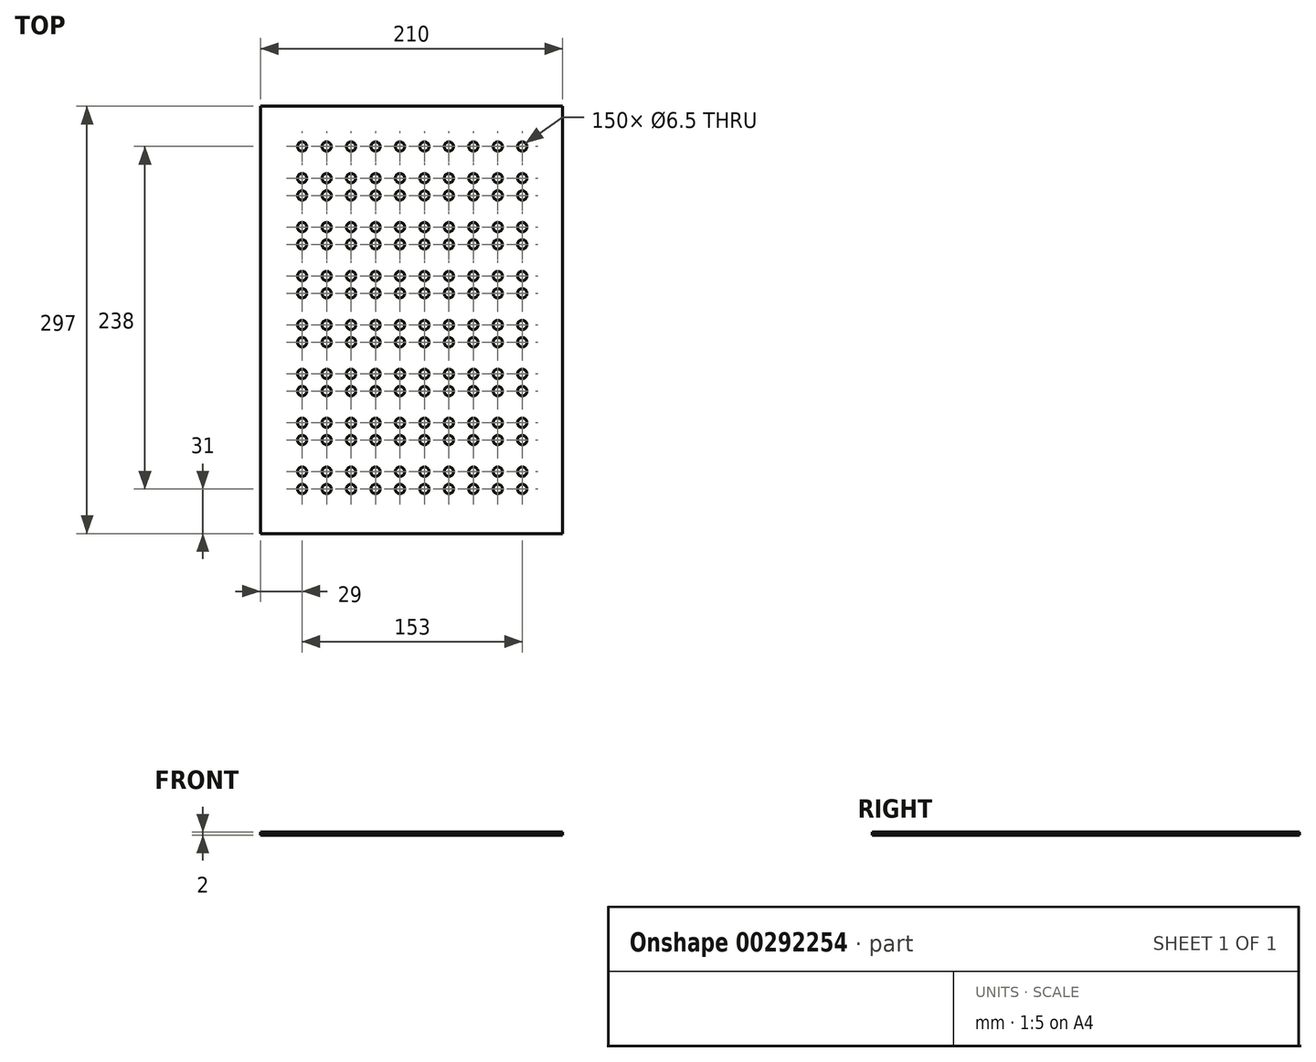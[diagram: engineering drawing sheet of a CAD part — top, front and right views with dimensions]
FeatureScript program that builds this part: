
annotation { "Feature Type Name" : "Feature", "Feature Type Description" : "" }
export const myFeature = defineFeature(function(context is Context, id is Id, definition is map)
    precondition{}
    {
        {
            var Q0;
            Q0=qCreatedBy(makeId("Top.planeOp"),FACE);
            var sketch = newSketch(context, id + "F0", { "sketchPlane" : qUnion([Q0])});
            skLineSegment(sketch, "E0.bottom", {"start": v(-105, 148.5) * mm, "end": v(105, 148.5) * mm});
            skLineSegment(sketch, "E0.top", {"start": v(-105, -148.5) * mm, "end": v(105, -148.5) * mm});
            skLineSegment(sketch, "E0.left", {"start": v(-105, 148.5) * mm, "end": v(-105, -148.5) * mm});
            skLineSegment(sketch, "E0.right", {"start": v(105, 148.5) * mm, "end": v(105, -148.5) * mm});
            skCircle(sketch, "E1", {"center": v(-76, 98.5) * mm, "radius": 3.25 * mm});
            skCircle(sketch, "E2.0.1.0", {"center": v(-76, 86.5) * mm, "radius": 3.25 * mm});
            skCircle(sketch, "E2.1.0.0", {"center": v(-59, 98.5) * mm, "radius": 3.25 * mm});
            skCircle(sketch, "E2.1.1.0", {"center": v(-59, 86.5) * mm, "radius": 3.25 * mm});
            skCircle(sketch, "E2.2.0.0", {"center": v(-42, 98.5) * mm, "radius": 3.25 * mm});
            skCircle(sketch, "E2.2.1.0", {"center": v(-42, 86.5) * mm, "radius": 3.25 * mm});
            skCircle(sketch, "E2.3.0.0", {"center": v(-25, 98.5) * mm, "radius": 3.25 * mm});
            skCircle(sketch, "E2.3.1.0", {"center": v(-25, 86.5) * mm, "radius": 3.25 * mm});
            skCircle(sketch, "E2.4.0.0", {"center": v(-8, 98.5) * mm, "radius": 3.25 * mm});
            skCircle(sketch, "E2.4.1.0", {"center": v(-8, 86.5) * mm, "radius": 3.25 * mm});
            skCircle(sketch, "E2.5.0.0", {"center": v(9, 98.5) * mm, "radius": 3.25 * mm});
            skCircle(sketch, "E2.5.1.0", {"center": v(9, 86.5) * mm, "radius": 3.25 * mm});
            skCircle(sketch, "E2.6.0.0", {"center": v(26, 98.5) * mm, "radius": 3.25 * mm});
            skCircle(sketch, "E2.6.1.0", {"center": v(26, 86.5) * mm, "radius": 3.25 * mm});
            skCircle(sketch, "E2.7.0.0", {"center": v(43, 98.5) * mm, "radius": 3.25 * mm});
            skCircle(sketch, "E2.7.1.0", {"center": v(43, 86.5) * mm, "radius": 3.25 * mm});
            skLineSegment(sketch, "E2.direction1", {"start": v(-76, 98.5) * mm, "end": v(-59, 98.5) * mm, "construction": true});
            skLineSegment(sketch, "E2.direction2", {"start": v(-76, 98.5) * mm, "end": v(-76, 86.5) * mm, "construction": true});
            skCircle(sketch, "E3", {"center": v(-76, 64.5) * mm, "radius": 3.25 * mm});
            skCircle(sketch, "E4.0.1.0", {"center": v(-76, 52.5) * mm, "radius": 3.25 * mm});
            skCircle(sketch, "E4.1.0.0", {"center": v(-59, 64.5) * mm, "radius": 3.25 * mm});
            skCircle(sketch, "E4.1.1.0", {"center": v(-59, 52.5) * mm, "radius": 3.25 * mm});
            skCircle(sketch, "E4.2.0.0", {"center": v(-42, 64.5) * mm, "radius": 3.25 * mm});
            skCircle(sketch, "E4.2.1.0", {"center": v(-42, 52.5) * mm, "radius": 3.25 * mm});
            skCircle(sketch, "E4.3.0.0", {"center": v(-25, 64.5) * mm, "radius": 3.25 * mm});
            skCircle(sketch, "E4.3.1.0", {"center": v(-25, 52.5) * mm, "radius": 3.25 * mm});
            skCircle(sketch, "E4.4.0.0", {"center": v(-8, 64.5) * mm, "radius": 3.25 * mm});
            skCircle(sketch, "E4.4.1.0", {"center": v(-8, 52.5) * mm, "radius": 3.25 * mm});
            skCircle(sketch, "E4.5.0.0", {"center": v(9, 64.5) * mm, "radius": 3.25 * mm});
            skCircle(sketch, "E4.5.1.0", {"center": v(9, 52.5) * mm, "radius": 3.25 * mm});
            skCircle(sketch, "E4.6.0.0", {"center": v(26, 64.5) * mm, "radius": 3.25 * mm});
            skCircle(sketch, "E4.6.1.0", {"center": v(26, 52.5) * mm, "radius": 3.25 * mm});
            skCircle(sketch, "E4.7.0.0", {"center": v(43, 64.5) * mm, "radius": 3.25 * mm});
            skCircle(sketch, "E4.7.1.0", {"center": v(43, 52.5) * mm, "radius": 3.25 * mm});
            skLineSegment(sketch, "E4.direction1", {"start": v(-76, 64.5) * mm, "end": v(-59, 64.5) * mm, "construction": true});
            skLineSegment(sketch, "E4.direction2", {"start": v(-76, 64.5) * mm, "end": v(-76, 52.5) * mm, "construction": true});
            skCircle(sketch, "E5", {"center": v(-76, 30.5) * mm, "radius": 3.25 * mm});
            skCircle(sketch, "E6.0.1.0", {"center": v(-76, 18.5) * mm, "radius": 3.25 * mm});
            skCircle(sketch, "E6.1.0.0", {"center": v(-59, 30.5) * mm, "radius": 3.25 * mm});
            skCircle(sketch, "E6.1.1.0", {"center": v(-59, 18.5) * mm, "radius": 3.25 * mm});
            skCircle(sketch, "E6.2.0.0", {"center": v(-42, 30.5) * mm, "radius": 3.25 * mm});
            skCircle(sketch, "E6.2.1.0", {"center": v(-42, 18.5) * mm, "radius": 3.25 * mm});
            skCircle(sketch, "E6.3.0.0", {"center": v(-25, 30.5) * mm, "radius": 3.25 * mm});
            skCircle(sketch, "E6.3.1.0", {"center": v(-25, 18.5) * mm, "radius": 3.25 * mm});
            skCircle(sketch, "E6.4.0.0", {"center": v(-8, 30.5) * mm, "radius": 3.25 * mm});
            skCircle(sketch, "E6.4.1.0", {"center": v(-8, 18.5) * mm, "radius": 3.25 * mm});
            skCircle(sketch, "E6.5.0.0", {"center": v(9, 30.5) * mm, "radius": 3.25 * mm});
            skCircle(sketch, "E6.5.1.0", {"center": v(9, 18.5) * mm, "radius": 3.25 * mm});
            skCircle(sketch, "E6.6.0.0", {"center": v(26, 30.5) * mm, "radius": 3.25 * mm});
            skCircle(sketch, "E6.6.1.0", {"center": v(26, 18.5) * mm, "radius": 3.25 * mm});
            skCircle(sketch, "E6.7.0.0", {"center": v(43, 30.5) * mm, "radius": 3.25 * mm});
            skCircle(sketch, "E6.7.1.0", {"center": v(43, 18.5) * mm, "radius": 3.25 * mm});
            skLineSegment(sketch, "E6.direction1", {"start": v(-76, 30.5) * mm, "end": v(-59, 30.5) * mm, "construction": true});
            skLineSegment(sketch, "E6.direction2", {"start": v(-76, 30.5) * mm, "end": v(-76, 18.5) * mm, "construction": true});
            skCircle(sketch, "E7", {"center": v(-76, -3.5) * mm, "radius": 3.25 * mm});
            skCircle(sketch, "E8.0.1.0", {"center": v(-76, -15.5) * mm, "radius": 3.25 * mm});
            skCircle(sketch, "E8.1.0.0", {"center": v(-59, -3.5) * mm, "radius": 3.25 * mm});
            skCircle(sketch, "E8.1.1.0", {"center": v(-59, -15.5) * mm, "radius": 3.25 * mm});
            skCircle(sketch, "E8.2.0.0", {"center": v(-42, -3.5) * mm, "radius": 3.25 * mm});
            skCircle(sketch, "E8.2.1.0", {"center": v(-42, -15.5) * mm, "radius": 3.25 * mm});
            skCircle(sketch, "E8.3.0.0", {"center": v(-25, -3.5) * mm, "radius": 3.25 * mm});
            skCircle(sketch, "E8.3.1.0", {"center": v(-25, -15.5) * mm, "radius": 3.25 * mm});
            skCircle(sketch, "E8.4.0.0", {"center": v(-8, -3.5) * mm, "radius": 3.25 * mm});
            skCircle(sketch, "E8.4.1.0", {"center": v(-8, -15.5) * mm, "radius": 3.25 * mm});
            skCircle(sketch, "E8.5.0.0", {"center": v(9, -3.5) * mm, "radius": 3.25 * mm});
            skCircle(sketch, "E8.5.1.0", {"center": v(9, -15.5) * mm, "radius": 3.25 * mm});
            skCircle(sketch, "E8.6.0.0", {"center": v(26, -3.5) * mm, "radius": 3.25 * mm});
            skCircle(sketch, "E8.6.1.0", {"center": v(26, -15.5) * mm, "radius": 3.25 * mm});
            skCircle(sketch, "E8.7.0.0", {"center": v(43, -3.5) * mm, "radius": 3.25 * mm});
            skCircle(sketch, "E8.7.1.0", {"center": v(43, -15.5) * mm, "radius": 3.25 * mm});
            skLineSegment(sketch, "E8.direction1", {"start": v(-76, -3.5) * mm, "end": v(-59, -3.5) * mm, "construction": true});
            skLineSegment(sketch, "E8.direction2", {"start": v(-76, -3.5) * mm, "end": v(-76, -15.5) * mm, "construction": true});
            skCircle(sketch, "E9", {"center": v(-76, -37.5) * mm, "radius": 3.25 * mm});
            skCircle(sketch, "E10.0.1.0", {"center": v(-76, -49.5) * mm, "radius": 3.25 * mm});
            skCircle(sketch, "E10.1.0.0", {"center": v(-59, -37.5) * mm, "radius": 3.25 * mm});
            skCircle(sketch, "E10.1.1.0", {"center": v(-59, -49.5) * mm, "radius": 3.25 * mm});
            skCircle(sketch, "E10.2.0.0", {"center": v(-42, -37.5) * mm, "radius": 3.25 * mm});
            skCircle(sketch, "E10.2.1.0", {"center": v(-42, -49.5) * mm, "radius": 3.25 * mm});
            skCircle(sketch, "E10.3.0.0", {"center": v(-25, -37.5) * mm, "radius": 3.25 * mm});
            skCircle(sketch, "E10.3.1.0", {"center": v(-25, -49.5) * mm, "radius": 3.25 * mm});
            skCircle(sketch, "E10.4.0.0", {"center": v(-8, -37.5) * mm, "radius": 3.25 * mm});
            skCircle(sketch, "E10.4.1.0", {"center": v(-8, -49.5) * mm, "radius": 3.25 * mm});
            skCircle(sketch, "E10.5.0.0", {"center": v(9, -37.5) * mm, "radius": 3.25 * mm});
            skCircle(sketch, "E10.5.1.0", {"center": v(9, -49.5) * mm, "radius": 3.25 * mm});
            skCircle(sketch, "E10.6.0.0", {"center": v(26, -37.5) * mm, "radius": 3.25 * mm});
            skCircle(sketch, "E10.6.1.0", {"center": v(26, -49.5) * mm, "radius": 3.25 * mm});
            skCircle(sketch, "E10.7.0.0", {"center": v(43, -37.5) * mm, "radius": 3.25 * mm});
            skCircle(sketch, "E10.7.1.0", {"center": v(43, -49.5) * mm, "radius": 3.25 * mm});
            skLineSegment(sketch, "E10.direction1", {"start": v(-76, -37.5) * mm, "end": v(-59, -37.5) * mm, "construction": true});
            skLineSegment(sketch, "E10.direction2", {"start": v(-76, -37.5) * mm, "end": v(-76, -49.5) * mm, "construction": true});
            skCircle(sketch, "E11", {"center": v(-76, 120.5) * mm, "radius": 3.25 * mm});
            skCircle(sketch, "E12.1.0.0", {"center": v(-59, 120.5) * mm, "radius": 3.25 * mm});
            skCircle(sketch, "E12.2.0.0", {"center": v(-42, 120.5) * mm, "radius": 3.25 * mm});
            skCircle(sketch, "E12.3.0.0", {"center": v(-25, 120.5) * mm, "radius": 3.25 * mm});
            skCircle(sketch, "E12.4.0.0", {"center": v(-8, 120.5) * mm, "radius": 3.25 * mm});
            skCircle(sketch, "E12.5.0.0", {"center": v(9, 120.5) * mm, "radius": 3.25 * mm});
            skCircle(sketch, "E12.6.0.0", {"center": v(26, 120.5) * mm, "radius": 3.25 * mm});
            skCircle(sketch, "E12.7.0.0", {"center": v(43, 120.5) * mm, "radius": 3.25 * mm});
            skLineSegment(sketch, "E12.direction1", {"start": v(-76, 120.5) * mm, "end": v(-59, 120.5) * mm, "construction": true});
            skCircle(sketch, "E13", {"center": v(-76, -71.5) * mm, "radius": 3.25 * mm});
            skCircle(sketch, "E14.0.1.0", {"center": v(-76, -83.5) * mm, "radius": 3.25 * mm});
            skCircle(sketch, "E14.1.0.0", {"center": v(-59, -71.5) * mm, "radius": 3.25 * mm});
            skCircle(sketch, "E14.1.1.0", {"center": v(-59, -83.5) * mm, "radius": 3.25 * mm});
            skCircle(sketch, "E14.2.0.0", {"center": v(-42, -71.5) * mm, "radius": 3.25 * mm});
            skCircle(sketch, "E14.2.1.0", {"center": v(-42, -83.5) * mm, "radius": 3.25 * mm});
            skCircle(sketch, "E14.3.0.0", {"center": v(-25, -71.5) * mm, "radius": 3.25 * mm});
            skCircle(sketch, "E14.3.1.0", {"center": v(-25, -83.5) * mm, "radius": 3.25 * mm});
            skCircle(sketch, "E14.4.0.0", {"center": v(-8, -71.5) * mm, "radius": 3.25 * mm});
            skCircle(sketch, "E14.4.1.0", {"center": v(-8, -83.5) * mm, "radius": 3.25 * mm});
            skCircle(sketch, "E14.5.0.0", {"center": v(9, -71.5) * mm, "radius": 3.25 * mm});
            skCircle(sketch, "E14.5.1.0", {"center": v(9, -83.5) * mm, "radius": 3.25 * mm});
            skCircle(sketch, "E14.6.0.0", {"center": v(26, -71.5) * mm, "radius": 3.25 * mm});
            skCircle(sketch, "E14.6.1.0", {"center": v(26, -83.5) * mm, "radius": 3.25 * mm});
            skCircle(sketch, "E14.7.0.0", {"center": v(43, -71.5) * mm, "radius": 3.25 * mm});
            skCircle(sketch, "E14.7.1.0", {"center": v(43, -83.5) * mm, "radius": 3.25 * mm});
            skCircle(sketch, "E14.8.0.0", {"center": v(60, -71.5) * mm, "radius": 3.25 * mm});
            skCircle(sketch, "E14.8.1.0", {"center": v(60, -83.5) * mm, "radius": 3.25 * mm});
            skCircle(sketch, "E14.9.0.0", {"center": v(77, -71.5) * mm, "radius": 3.25 * mm});
            skCircle(sketch, "E14.9.1.0", {"center": v(77, -83.5) * mm, "radius": 3.25 * mm});
            skLineSegment(sketch, "E14.direction1", {"start": v(-76, -71.5) * mm, "end": v(-59, -71.5) * mm, "construction": true});
            skLineSegment(sketch, "E14.direction2", {"start": v(-76, -71.5) * mm, "end": v(-76, -83.5) * mm, "construction": true});
            skCircle(sketch, "E15.0.8.0", {"center": v(60, -3.5) * mm, "radius": 3.25 * mm});
            skCircle(sketch, "E15.0.8.1", {"center": v(60, -15.5) * mm, "radius": 3.25 * mm});
            skCircle(sketch, "E15.0.9.0", {"center": v(77, -3.5) * mm, "radius": 3.25 * mm});
            skCircle(sketch, "E15.0.9.1", {"center": v(77, -15.5) * mm, "radius": 3.25 * mm});
            skCircle(sketch, "E16.0.8.0", {"center": v(60, 30.5) * mm, "radius": 3.25 * mm});
            skCircle(sketch, "E16.0.8.1", {"center": v(60, 18.5) * mm, "radius": 3.25 * mm});
            skCircle(sketch, "E16.0.9.0", {"center": v(77, 30.5) * mm, "radius": 3.25 * mm});
            skCircle(sketch, "E16.0.9.1", {"center": v(77, 18.5) * mm, "radius": 3.25 * mm});
            skCircle(sketch, "E17.0.8.0", {"center": v(60, -37.5) * mm, "radius": 3.25 * mm});
            skCircle(sketch, "E17.0.8.1", {"center": v(60, -49.5) * mm, "radius": 3.25 * mm});
            skCircle(sketch, "E17.0.9.0", {"center": v(77, -37.5) * mm, "radius": 3.25 * mm});
            skCircle(sketch, "E17.0.9.1", {"center": v(77, -49.5) * mm, "radius": 3.25 * mm});
            skCircle(sketch, "E18.0.8.0", {"center": v(60, 64.5) * mm, "radius": 3.25 * mm});
            skCircle(sketch, "E18.0.8.1", {"center": v(60, 52.5) * mm, "radius": 3.25 * mm});
            skCircle(sketch, "E18.0.9.0", {"center": v(77, 64.5) * mm, "radius": 3.25 * mm});
            skCircle(sketch, "E18.0.9.1", {"center": v(77, 52.5) * mm, "radius": 3.25 * mm});
            skCircle(sketch, "E19.0.8.0", {"center": v(60, 98.5) * mm, "radius": 3.25 * mm});
            skCircle(sketch, "E19.0.8.1", {"center": v(60, 86.5) * mm, "radius": 3.25 * mm});
            skCircle(sketch, "E19.0.9.0", {"center": v(77, 98.5) * mm, "radius": 3.25 * mm});
            skCircle(sketch, "E19.0.9.1", {"center": v(77, 86.5) * mm, "radius": 3.25 * mm});
            skCircle(sketch, "E20.0.8.0", {"center": v(60, 120.5) * mm, "radius": 3.25 * mm});
            skCircle(sketch, "E20.0.9.0", {"center": v(77, 120.5) * mm, "radius": 3.25 * mm});
            skCircle(sketch, "E21", {"center": v(-76, -105.5) * mm, "radius": 3.25 * mm});
            skCircle(sketch, "E22.0.1.0", {"center": v(-76, -117.5) * mm, "radius": 3.25 * mm});
            skCircle(sketch, "E22.1.0.0", {"center": v(-59, -105.5) * mm, "radius": 3.25 * mm});
            skCircle(sketch, "E22.1.1.0", {"center": v(-59, -117.5) * mm, "radius": 3.25 * mm});
            skCircle(sketch, "E22.2.0.0", {"center": v(-42, -105.5) * mm, "radius": 3.25 * mm});
            skCircle(sketch, "E22.2.1.0", {"center": v(-42, -117.5) * mm, "radius": 3.25 * mm});
            skCircle(sketch, "E22.3.0.0", {"center": v(-25, -105.5) * mm, "radius": 3.25 * mm});
            skCircle(sketch, "E22.3.1.0", {"center": v(-25, -117.5) * mm, "radius": 3.25 * mm});
            skCircle(sketch, "E22.4.0.0", {"center": v(-8, -105.5) * mm, "radius": 3.25 * mm});
            skCircle(sketch, "E22.4.1.0", {"center": v(-8, -117.5) * mm, "radius": 3.25 * mm});
            skCircle(sketch, "E22.5.0.0", {"center": v(9, -105.5) * mm, "radius": 3.25 * mm});
            skCircle(sketch, "E22.5.1.0", {"center": v(9, -117.5) * mm, "radius": 3.25 * mm});
            skCircle(sketch, "E22.6.0.0", {"center": v(26, -105.5) * mm, "radius": 3.25 * mm});
            skCircle(sketch, "E22.6.1.0", {"center": v(26, -117.5) * mm, "radius": 3.25 * mm});
            skCircle(sketch, "E22.7.0.0", {"center": v(43, -105.5) * mm, "radius": 3.25 * mm});
            skCircle(sketch, "E22.7.1.0", {"center": v(43, -117.5) * mm, "radius": 3.25 * mm});
            skCircle(sketch, "E22.8.0.0", {"center": v(60, -105.5) * mm, "radius": 3.25 * mm});
            skCircle(sketch, "E22.8.1.0", {"center": v(60, -117.5) * mm, "radius": 3.25 * mm});
            skCircle(sketch, "E22.9.0.0", {"center": v(77, -105.5) * mm, "radius": 3.25 * mm});
            skCircle(sketch, "E22.9.1.0", {"center": v(77, -117.5) * mm, "radius": 3.25 * mm});
            skLineSegment(sketch, "E22.direction1", {"start": v(-76, -105.5) * mm, "end": v(-59, -105.5) * mm, "construction": true});
            skLineSegment(sketch, "E22.direction2", {"start": v(-76, -105.5) * mm, "end": v(-76, -117.5) * mm, "construction": true});
            skSolve(sketch);
        }
        {
            var Q0;
            Q0=makeQuery(id+"F0.imprint","IMPRINT",FACE,{"disambiguationData":[TD([[makeQuery(id+"F0.imprint","IMPRINT",EDGE,{"derivedFrom":sQuery(id+"F0.wireOp",EDGE,"E0.bottom")}),-1.0]])]});
            extrude(context, id + "F1", {"entities" : qUnion([Q0]), "depth" : 2 * mm});
        }
    });
